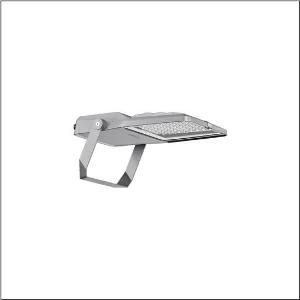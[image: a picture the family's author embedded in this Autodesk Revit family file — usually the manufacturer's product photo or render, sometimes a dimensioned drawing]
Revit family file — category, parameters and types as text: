
# Revit family: floodlight_fl_21_iq_mini___rs12_5xa7771d2b1a_498a
name_source: partatom
category: Lighting Fixtures
units: mm (PartAtom-declared; Revit-internal decimal feet)

## family parameters
Cut with Voids When Loaded = No
Host = Face
Light Source = No
Part Type = Normal
Room Calculation Point = No
Round Connector Dimension = Use Diameter
Shared = No

## types (1)
- --- (1 x LED, 18020 lm, 143 W, 3000K)
    Apparent Load = 143 VA
    CIE Flux Codes = 79 92 99 100 100
    Color Rendering = 70
    Color Temperature = 3000K
    Default Elevation = 1800 mm
    Description = Floodlight FL 21 iQ mini, floodlight, primary light control with lens, of PMMA, primary optical cover: protective disc, of toughened safety glass, transparent, light distribution: RS12, light emission: direct distribution, installation type: surface-mounted, LED, High Power LED, rated luminous flux: 18.020lm, luminous efficacy: 126lm/W, light colour: 730, colour temperature: 3000K, control: Auto-Match, Temp-Guard, Lumen-Switch, Night-Set, Smart-Wire, Light-Fading, Desk-Remote (wireless, voltage-free reading and setting of iQ features in the workshop via application-optimized NFC function/RFID function), optimised constant luminous flux control (CLO 2.0), with terminal, 6-pole, mains connection: 220..240V, AC, 50/60Hz, start of lifetime: 143W, end of service life: 152W, reduction: 61W, luminaire housing, of diecast aluminium, powder-coated, Siteco® metallic grey (DB 702S), corrosivity category C5 mid according to DIN EN ISO 12944, sealing non-destructively replaceable, mounting bracket, of steel, galvanised, powder-coated, Siteco® metallic grey (DB 702S), protection rating (complete): IP66, insulation class (complete): insulation class II (safety insulation), certification: CE, ENEC, VDE, protection symbol: D, impact resistance: IK08, permissible operating ambient temperature: -40..+40°C, permissible operating ambient temperature for outdoor applications: -40..+50°C, standard: DIN EN 12944, LABS conformity tested according to VDMA 24364:2018-05, packaging unit: 1 piece

Light Distribution: RS12
    Height = 70 mm
    Lamp = 1 x LED
    Lamp Light Flux = 18020 lm
    Lamp Power = 143 W
    Lamp count = 1
    Length = 485 mm
    Luminous efficacy = 126 lm/W
    Manufacturer = Siteco
    ModVariant = No
    Model = 5XA7771D2B1A
    Number of Poles = 1
    OnlyDefault = Yes
    Power Factor = 1
    Product Name = Floodlight FL 21 iQ mini | RS12
    Product group = floodlight | pylon annexe
    ProductGroupID = 6200
    Protection Class = Protection class II
    Protection Degree = IP 66
    RLX_Detail_Level = 1
    RLX_Emergency_Light_Flux = 0 lm
    RLX_Emergency_Type = 0
    RLX_Emergency_Type_DB = No
    RlxData = <blob elided: 91097 chars, md5=69ff5807>
    Socket = socket
    Standby Power = 0 W
    System Light Flux = 18020 lm
    System Power = 143 W
    Type Comments = factory setting: luminous flux: 100 % | dim-lin: 254 | 730 mA
    Type Image = l_1006845.jpg
    URL = http://relux.com
    VarID = @adj_117657
    Voltage = 0 V
    Weight = 0.00 kg
    Width = 337 mm

## geometry (parser evidence)
native form markers: Blend x4, Sweep x14
no freeform markers — native parametric forms only
